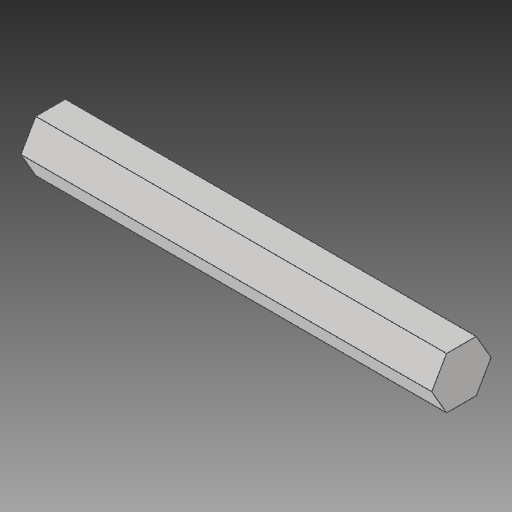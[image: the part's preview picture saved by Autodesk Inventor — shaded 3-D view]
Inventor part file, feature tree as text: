
AUTODESK INVENTOR PART (.ipt)
format: ipt  version: 2018 (Build 220112000, 112)  size: 94,720 bytes
history: native  units: in
note: dims shown in document units (in); Inventor stores cm internally (conversion verified against a paired STEP export)
features: extrude x1, sketch x1
ambient origin geometry x8: Origin, YZ Plane, XZ Plane, XY Plane, X Axis, Y Axis, Z Axis, Center Point
bodies: Solid1 (feature_tree)
feature tree (2):
  extrude  "Extrusion1"  Depth=4.0in TaperAngle=0.0deg
  sketch  "Sketch1"  dims[d0=0.25in d1=4.0in d2=0.0in]
